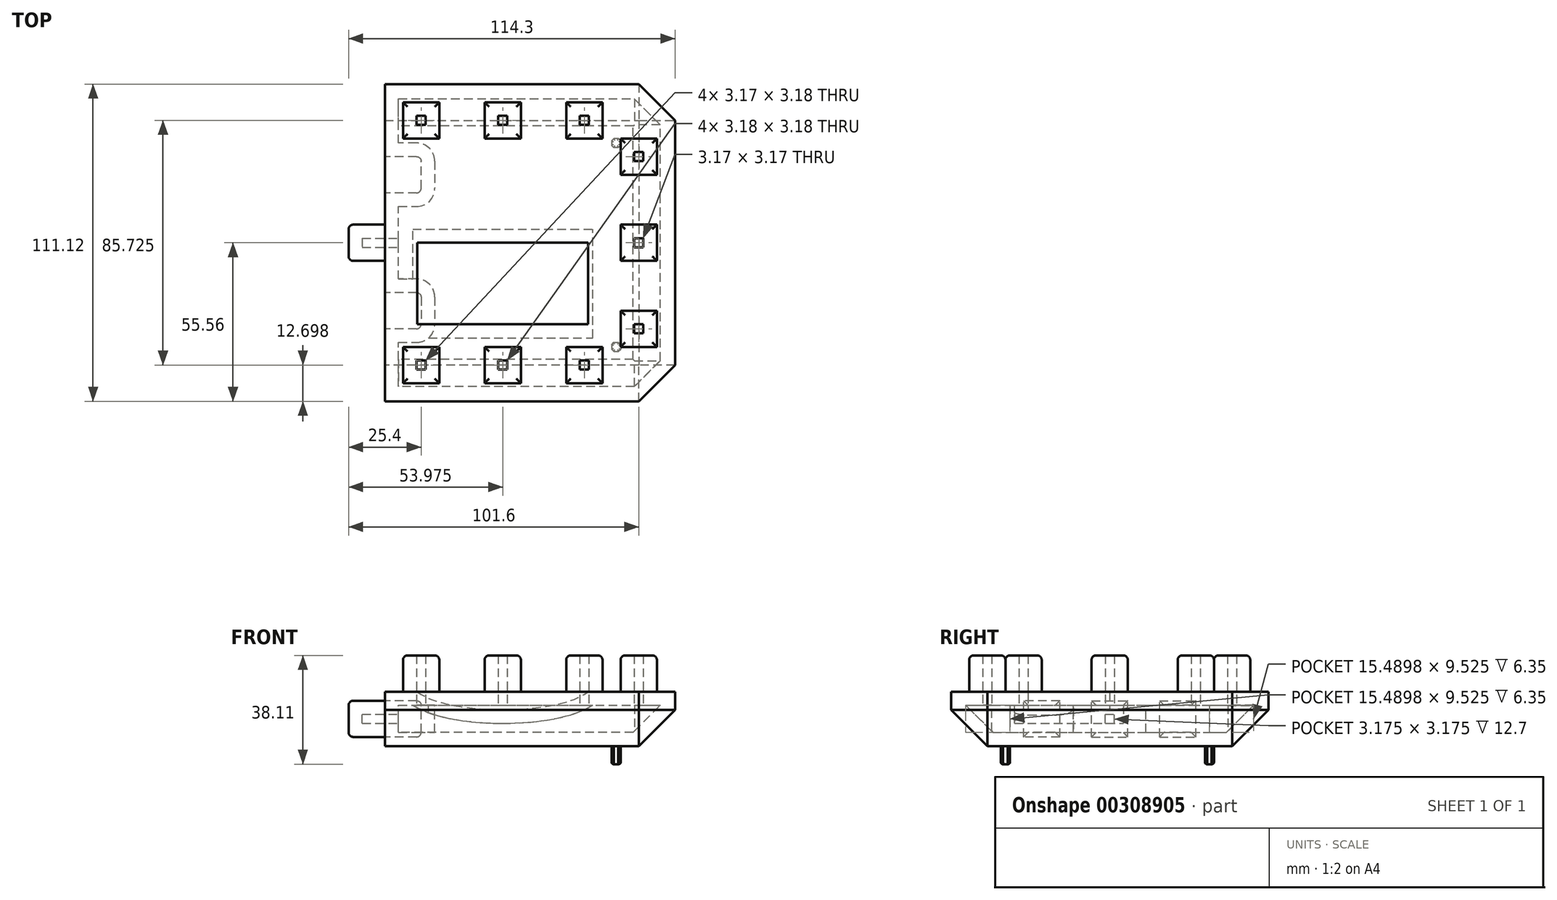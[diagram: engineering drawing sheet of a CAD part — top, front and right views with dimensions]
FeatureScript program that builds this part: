
annotation { "Feature Type Name" : "Feature", "Feature Type Description" : "" }
export const myFeature = defineFeature(function(context is Context, id is Id, definition is map)
    precondition{}
    {
        {
            var Q0;
            Q0=qCreatedBy(makeId("Front.planeOp"),FACE);
            var sketch = newSketch(context, id + "F0", { "sketchPlane" : qUnion([Q0])});
            skLineSegment(sketch, "E0.bottom", {"start": v(-50.8, -9.53) * mm, "end": v(50.8, -9.53) * mm});
            skLineSegment(sketch, "E0.top", {"start": v(-50.8, 9.53) * mm, "end": v(50.8, 9.53) * mm});
            skLineSegment(sketch, "E0.left", {"start": v(-50.8, -9.53) * mm, "end": v(-50.8, 9.53) * mm});
            skLineSegment(sketch, "E0.right", {"start": v(50.8, -9.53) * mm, "end": v(50.8, 9.53) * mm});
            skPoint(sketch, "E0.middle", {"position": v(0, 0) * mm});
            skSolve(sketch);
        }
        {
            var Q0;
            Q0=qSketchRegion(id+"F0",true);
            extrude(context, id + "F1", {"entities" : qUnion([Q0]), "endBound" : BoundingType.SYMMETRIC, "depth" : 111.12 * mm});
        }
        {
            var Q0;
            Q0=makeQuery(id+"F1.opExtrude","SWEPT_EDGE",EDGE,{"disambiguationData":[OSD([sQuery(id+"F0.wireOp",EDGE,"E0.bottom"),sQuery(id+"F0.wireOp",EDGE,"E0.right")])]});
            var Q1;
            Q1=makeQuery(id+"F1.opExtrude","CAP_EDGE",EDGE,{"disambiguationData":[OSD([sQuery(id+"F0.wireOp",EDGE,"E0.bottom")])],"isStart":false});
            var Q2;
            Q2=makeQuery(id+"F1.opExtrude","CAP_EDGE",EDGE,{"disambiguationData":[OSD([sQuery(id+"F0.wireOp",EDGE,"E0.bottom")])],"isStart":true});
            var Q3;
            Q3=makeQuery(id+"F1.opExtrude","CAP_EDGE",EDGE,{"disambiguationData":[OSD([sQuery(id+"F0.wireOp",EDGE,"E0.right")])],"isStart":false});
            var Q4;
            Q4=makeQuery(id+"F1.opExtrude","CAP_EDGE",EDGE,{"disambiguationData":[OSD([sQuery(id+"F0.wireOp",EDGE,"E0.right")])],"isStart":true});
            chamfer(context, id + "F2", {"entities" : qUnion([Q0, Q1, Q2, Q3, Q4]), "width" : 12.7 * mm, "tangentPropagation" : true});
        }
        {
            var Q0;
            Q0=makeQuery(id+"F1.opExtrude","SWEPT_FACE",FACE,{"disambiguationData":[OSD([sQuery(id+"F0.wireOp",EDGE,"E0.top")])]});
            var sketch = newSketch(context, id + "F3", { "sketchPlane" : qUnion([Q0])});
            skLineSegment(sketch, "E1.bottom", {"start": v(31.75, 23.81) * mm, "end": v(44.45, 23.81) * mm});
            skLineSegment(sketch, "E1.top", {"start": v(31.75, 36.51) * mm, "end": v(44.45, 36.51) * mm});
            skLineSegment(sketch, "E1.left", {"start": v(31.75, 23.81) * mm, "end": v(31.75, 36.51) * mm});
            skLineSegment(sketch, "E1.right", {"start": v(44.45, 23.81) * mm, "end": v(44.45, 36.51) * mm});
            skPoint(sketch, "E1.middle", {"position": v(38.1, 30.16) * mm});
            skLineSegment(sketch, "E2.bottom", {"start": v(31.75, -36.51) * mm, "end": v(44.45, -36.51) * mm});
            skLineSegment(sketch, "E2.top", {"start": v(31.75, -23.81) * mm, "end": v(44.45, -23.81) * mm});
            skLineSegment(sketch, "E2.left", {"start": v(31.75, -36.51) * mm, "end": v(31.75, -23.81) * mm});
            skLineSegment(sketch, "E2.right", {"start": v(44.45, -36.51) * mm, "end": v(44.45, -23.81) * mm});
            skPoint(sketch, "E2.middle", {"position": v(38.1, -30.16) * mm});
            skLineSegment(sketch, "E3.bottom", {"start": v(31.75, -6.35) * mm, "end": v(44.45, -6.35) * mm});
            skLineSegment(sketch, "E3.top", {"start": v(31.75, 6.35) * mm, "end": v(44.45, 6.35) * mm});
            skLineSegment(sketch, "E3.left", {"start": v(31.75, -6.35) * mm, "end": v(31.75, 6.35) * mm});
            skLineSegment(sketch, "E3.right", {"start": v(44.45, -6.35) * mm, "end": v(44.45, 6.35) * mm});
            skPoint(sketch, "E3.middle", {"position": v(38.1, 0) * mm});
            skLineSegment(sketch, "E4.bottom", {"start": v(12.7, 36.51) * mm, "end": v(25.4, 36.51) * mm});
            skLineSegment(sketch, "E4.top", {"start": v(12.7, 49.21) * mm, "end": v(25.4, 49.21) * mm});
            skLineSegment(sketch, "E4.left", {"start": v(12.7, 36.51) * mm, "end": v(12.7, 49.21) * mm});
            skLineSegment(sketch, "E4.right", {"start": v(25.4, 36.51) * mm, "end": v(25.4, 49.21) * mm});
            skPoint(sketch, "E4.middle", {"position": v(19.05, 42.86) * mm});
            skLineSegment(sketch, "E5.bottom", {"start": v(12.7, -36.51) * mm, "end": v(25.4, -36.51) * mm});
            skLineSegment(sketch, "E5.top", {"start": v(12.7, -49.21) * mm, "end": v(25.4, -49.21) * mm});
            skLineSegment(sketch, "E5.left", {"start": v(12.7, -36.51) * mm, "end": v(12.7, -49.21) * mm});
            skLineSegment(sketch, "E5.right", {"start": v(25.4, -36.51) * mm, "end": v(25.4, -49.21) * mm});
            skPoint(sketch, "E5.middle", {"position": v(19.05, -42.86) * mm});
            skLineSegment(sketch, "E6.bottom", {"start": v(-15.88, 36.51) * mm, "end": v(-3.17, 36.51) * mm});
            skLineSegment(sketch, "E6.top", {"start": v(-15.88, 49.21) * mm, "end": v(-3.17, 49.21) * mm});
            skLineSegment(sketch, "E6.left", {"start": v(-15.88, 36.51) * mm, "end": v(-15.88, 49.21) * mm});
            skLineSegment(sketch, "E6.right", {"start": v(-3.18, 36.51) * mm, "end": v(-3.18, 49.21) * mm});
            skPoint(sketch, "E6.middle", {"position": v(-9.53, 42.86) * mm});
            skLineSegment(sketch, "E7.bottom", {"start": v(-15.88, -36.51) * mm, "end": v(-3.17, -36.51) * mm});
            skLineSegment(sketch, "E7.top", {"start": v(-15.88, -49.21) * mm, "end": v(-3.17, -49.21) * mm});
            skLineSegment(sketch, "E7.left", {"start": v(-15.88, -36.51) * mm, "end": v(-15.88, -49.21) * mm});
            skLineSegment(sketch, "E7.right", {"start": v(-3.18, -36.51) * mm, "end": v(-3.18, -49.21) * mm});
            skPoint(sketch, "E7.middle", {"position": v(-9.52, -42.86) * mm});
            skLineSegment(sketch, "E8.bottom", {"start": v(-31.75, 36.51) * mm, "end": v(-44.45, 36.51) * mm});
            skLineSegment(sketch, "E8.top", {"start": v(-31.75, 49.21) * mm, "end": v(-44.45, 49.21) * mm});
            skLineSegment(sketch, "E8.left", {"start": v(-31.75, 36.51) * mm, "end": v(-31.75, 49.21) * mm});
            skLineSegment(sketch, "E8.right", {"start": v(-44.45, 36.51) * mm, "end": v(-44.45, 49.21) * mm});
            skPoint(sketch, "E8.middle", {"position": v(-38.1, 42.86) * mm});
            skPoint(sketch, "E8.middle.positionSnap0", {"position": v(-15.88, 42.86) * mm});
            skPoint(sketch, "E8.centerSnap0", {"position": v(-15.88, 42.86) * mm});
            skLineSegment(sketch, "E9.bottom", {"start": v(-31.75, -49.21) * mm, "end": v(-44.45, -49.21) * mm});
            skLineSegment(sketch, "E9.top", {"start": v(-31.75, -36.51) * mm, "end": v(-44.45, -36.51) * mm});
            skLineSegment(sketch, "E9.left", {"start": v(-31.75, -49.21) * mm, "end": v(-31.75, -36.51) * mm});
            skLineSegment(sketch, "E9.right", {"start": v(-44.45, -49.21) * mm, "end": v(-44.45, -36.51) * mm});
            skPoint(sketch, "E9.middle", {"position": v(-38.1, -42.86) * mm});
            skPoint(sketch, "E9.middle.positionSnap0", {"position": v(-15.88, -42.86) * mm});
            skPoint(sketch, "E9.centerSnap0", {"position": v(-15.88, -42.86) * mm});
            skSolve(sketch);
        }
        {
            var Q0;
            Q0=qSketchRegion(id+"F3",true);
            extrude(context, id + "F4", {"entities" : qUnion([Q0]), "operationType" : NewBodyOperationType.ADD, "depth" : 12.7 * mm});
        }
        {
            var Q0;
            Q0=makeQuery(id+"F1.opExtrude","SWEPT_FACE",FACE,{"disambiguationData":[OSD([sQuery(id+"F0.wireOp",EDGE,"E0.bottom")])]});
            var sketch = newSketch(context, id + "F5", { "sketchPlane" : qUnion([Q0])});
            skLineSegment(sketch, "E10.bottom", {"start": v(28.58, 34.93) * mm, "end": v(31.75, 34.93) * mm});
            skLineSegment(sketch, "E10.top", {"start": v(28.58, 38.1) * mm, "end": v(31.75, 38.1) * mm});
            skLineSegment(sketch, "E10.left", {"start": v(28.58, 34.93) * mm, "end": v(28.58, 38.1) * mm});
            skLineSegment(sketch, "E10.right", {"start": v(31.75, 34.93) * mm, "end": v(31.75, 38.1) * mm});
            skPoint(sketch, "E10.middle", {"position": v(30.16, 36.51) * mm});
            skLineSegment(sketch, "E11.bottom", {"start": v(31.75, -36.51) * mm, "end": v(28.58, -36.51) * mm});
            skLineSegment(sketch, "E11.top", {"start": v(31.75, -33.34) * mm, "end": v(28.58, -33.34) * mm});
            skLineSegment(sketch, "E11.left", {"start": v(31.75, -36.51) * mm, "end": v(31.75, -33.34) * mm});
            skLineSegment(sketch, "E11.right", {"start": v(28.58, -36.51) * mm, "end": v(28.58, -33.34) * mm});
            skPoint(sketch, "E11.middle", {"position": v(30.16, -34.92) * mm});
            skSolve(sketch);
        }
        {
            var Q0;
            Q0=qSketchRegion(id+"F5",true);
            extrude(context, id + "F6", {"entities" : qUnion([Q0]), "operationType" : NewBodyOperationType.ADD, "depth" : 6.35 * mm});
        }
        {
            var Q0;
            Q0=makeQuery(id+"F6.opExtrude","SWEPT_EDGE",EDGE,{"disambiguationData":[OSD([sQuery(id+"F5.wireOp",EDGE,"E11.bottom"),sQuery(id+"F5.wireOp",EDGE,"E11.right")])]});
            var Q1;
            Q1=makeQuery(id+"F6.opExtrude","SWEPT_EDGE",EDGE,{"disambiguationData":[OSD([sQuery(id+"F5.wireOp",EDGE,"E11.top"),sQuery(id+"F5.wireOp",EDGE,"E11.right")])]});
            var Q2;
            Q2=makeQuery(id+"F6.opExtrude","SWEPT_EDGE",EDGE,{"disambiguationData":[OSD([sQuery(id+"F5.wireOp",EDGE,"E11.top"),sQuery(id+"F5.wireOp",EDGE,"E11.left")])]});
            var Q3;
            Q3=makeQuery(id+"F6.opExtrude","SWEPT_EDGE",EDGE,{"disambiguationData":[OSD([sQuery(id+"F5.wireOp",EDGE,"E11.bottom"),sQuery(id+"F5.wireOp",EDGE,"E11.left")])]});
            var Q4;
            Q4=makeQuery(id+"F6.opExtrude","CAP_EDGE",EDGE,{"disambiguationData":[OSD([sQuery(id+"F5.wireOp",EDGE,"E11.left")])],"isStart":true});
            var Q5;
            Q5=makeQuery(id+"F6.opExtrude","SWEPT_EDGE",EDGE,{"disambiguationData":[OSD([sQuery(id+"F5.wireOp",EDGE,"E10.bottom"),sQuery(id+"F5.wireOp",EDGE,"E10.left")])]});
            var Q6;
            Q6=makeQuery(id+"F6.opExtrude","SWEPT_EDGE",EDGE,{"disambiguationData":[OSD([sQuery(id+"F5.wireOp",EDGE,"E10.bottom"),sQuery(id+"F5.wireOp",EDGE,"E10.right")])]});
            var Q7;
            Q7=makeQuery(id+"F6.opExtrude","SWEPT_EDGE",EDGE,{"disambiguationData":[OSD([sQuery(id+"F5.wireOp",EDGE,"E10.top"),sQuery(id+"F5.wireOp",EDGE,"E10.right")])]});
            var Q8;
            Q8=makeQuery(id+"F6.opExtrude","CAP_EDGE",EDGE,{"disambiguationData":[OSD([sQuery(id+"F5.wireOp",EDGE,"E10.right")])],"isStart":true});
            var Q9;
            Q9=makeQuery(id+"F6.opExtrude","SWEPT_EDGE",EDGE,{"disambiguationData":[OSD([sQuery(id+"F5.wireOp",EDGE,"E10.top"),sQuery(id+"F5.wireOp",EDGE,"E10.left")])]});
            chamfer(context, id + "F7", {"entities" : qUnion([Q0, Q1, Q2, Q3, Q4, Q5, Q6, Q7, Q8, Q9]), "width" : 0.8 * mm, "tangentPropagation" : true});
        }
        {
            var Q0;
            Q0=makeQuery(id+"F6.opExtrude","CAP_FACE",FACE,{"disambiguationData":[OSD([sQuery(id+"F5.wireOp",EDGE,"E10.bottom"),sQuery(id+"F5.wireOp",EDGE,"E10.top"),sQuery(id+"F5.wireOp",EDGE,"E10.left"),sQuery(id+"F5.wireOp",EDGE,"E10.right")])],"isStart":false});
            var Q1;
            Q1=makeQuery(id+"F6.opExtrude","CAP_FACE",FACE,{"disambiguationData":[OSD([sQuery(id+"F5.wireOp",EDGE,"E11.bottom"),sQuery(id+"F5.wireOp",EDGE,"E11.top"),sQuery(id+"F5.wireOp",EDGE,"E11.left"),sQuery(id+"F5.wireOp",EDGE,"E11.right")])],"isStart":false});
            fillet(context, id + "F8", {"entities" : qUnion([Q0, Q1]), "radius" : 0.64 * mm, "tangentPropagation" : true, "allowEdgeOverflow" : false});
        }
        {
            var Q0;
            Q0=makeQuery(id+"F1.opExtrude","SWEPT_FACE",FACE,{"disambiguationData":[OSD([sQuery(id+"F0.wireOp",EDGE,"E0.left")])]});
            var sketch = newSketch(context, id + "F9", { "sketchPlane" : qUnion([Q0])});
            skLineSegment(sketch, "E12.bottom", {"start": v(-17.46, -6.35) * mm, "end": v(-30.16, -6.35) * mm});
            skLineSegment(sketch, "E12.top", {"start": v(-17.46, 6.35) * mm, "end": v(-30.16, 6.35) * mm});
            skLineSegment(sketch, "E12.left", {"start": v(-17.46, -6.35) * mm, "end": v(-17.46, 6.35) * mm});
            skLineSegment(sketch, "E12.right", {"start": v(-30.16, -6.35) * mm, "end": v(-30.16, 6.35) * mm});
            skPoint(sketch, "E12.middle", {"position": v(-23.81, 0) * mm});
            skLineSegment(sketch, "E13.bottom", {"start": v(17.46, -6.35) * mm, "end": v(30.16, -6.35) * mm});
            skLineSegment(sketch, "E13.top", {"start": v(17.46, 6.35) * mm, "end": v(30.16, 6.35) * mm});
            skLineSegment(sketch, "E13.left", {"start": v(17.46, -6.35) * mm, "end": v(17.46, 6.35) * mm});
            skLineSegment(sketch, "E13.right", {"start": v(30.16, -6.35) * mm, "end": v(30.16, 6.35) * mm});
            skPoint(sketch, "E13.middle", {"position": v(23.81, 0) * mm});
            skLineSegment(sketch, "E14.bottom", {"start": v(6.35, -6.35) * mm, "end": v(-6.35, -6.35) * mm});
            skLineSegment(sketch, "E14.top", {"start": v(6.35, 6.35) * mm, "end": v(-6.35, 6.35) * mm});
            skLineSegment(sketch, "E14.left", {"start": v(6.35, -6.35) * mm, "end": v(6.35, 6.35) * mm});
            skLineSegment(sketch, "E14.right", {"start": v(-6.35, -6.35) * mm, "end": v(-6.35, 6.35) * mm});
            skPoint(sketch, "E14.middle", {"position": v(0, 0) * mm});
            skSolve(sketch);
        }
        {
            var Q0;
            Q0=makeQuery(id+"F9.imprint","IMPRINT",FACE,{"disambiguationData":[TD([[makeQuery(id+"F9.imprint","IMPRINT",EDGE,{"derivedFrom":sQuery(id+"F9.wireOp",EDGE,"E12.bottom")}),-1.0]])]});
            var Q1;
            Q1=makeQuery(id+"F9.imprint","IMPRINT",FACE,{"disambiguationData":[TD([[makeQuery(id+"F9.imprint","IMPRINT",EDGE,{"derivedFrom":sQuery(id+"F9.wireOp",EDGE,"E13.bottom")}),1.0]])]});
            extrude(context, id + "F10", {"entities" : qUnion([Q0, Q1]), "operationType" : NewBodyOperationType.REMOVE, "oppositeDirection" : true, "depth" : 12.7 * mm});
        }
        {
            var Q0;
            Q0=makeQuery(id+"F9.imprint","IMPRINT",FACE,{"disambiguationData":[TD([[makeQuery(id+"F9.imprint","IMPRINT",EDGE,{"derivedFrom":sQuery(id+"F9.wireOp",EDGE,"E14.bottom")}),-1.0]])]});
            extrude(context, id + "F11", {"entities" : qUnion([Q0]), "operationType" : NewBodyOperationType.ADD, "depth" : 12.7 * mm});
        }
        {
            var Q0;
            Q0=makeQuery(id+"F4.opExtrude","CAP_FACE",FACE,{"disambiguationData":[OSD([sQuery(id+"F3.wireOp",EDGE,"E1.bottom"),sQuery(id+"F3.wireOp",EDGE,"E1.top"),sQuery(id+"F3.wireOp",EDGE,"E1.left"),sQuery(id+"F3.wireOp",EDGE,"E1.right")])],"isStart":false});
            var Q1;
            Q1=makeQuery(id+"F4.opExtrude","CAP_FACE",FACE,{"disambiguationData":[OSD([sQuery(id+"F3.wireOp",EDGE,"E3.bottom"),sQuery(id+"F3.wireOp",EDGE,"E3.top"),sQuery(id+"F3.wireOp",EDGE,"E3.left"),sQuery(id+"F3.wireOp",EDGE,"E3.right")])],"isStart":false});
            var Q2;
            Q2=makeQuery(id+"F4.opExtrude","CAP_FACE",FACE,{"disambiguationData":[OSD([sQuery(id+"F3.wireOp",EDGE,"E2.bottom"),sQuery(id+"F3.wireOp",EDGE,"E2.top"),sQuery(id+"F3.wireOp",EDGE,"E2.left"),sQuery(id+"F3.wireOp",EDGE,"E2.right")])],"isStart":false});
            var Q3;
            Q3=makeQuery(id+"F4.opExtrude","CAP_FACE",FACE,{"disambiguationData":[OSD([sQuery(id+"F3.wireOp",EDGE,"E4.bottom"),sQuery(id+"F3.wireOp",EDGE,"E4.top"),sQuery(id+"F3.wireOp",EDGE,"E4.left"),sQuery(id+"F3.wireOp",EDGE,"E4.right")])],"isStart":false});
            var Q4;
            Q4=makeQuery(id+"F4.opExtrude","CAP_FACE",FACE,{"disambiguationData":[OSD([sQuery(id+"F3.wireOp",EDGE,"E6.bottom"),sQuery(id+"F3.wireOp",EDGE,"E6.top"),sQuery(id+"F3.wireOp",EDGE,"E6.left"),sQuery(id+"F3.wireOp",EDGE,"E6.right")])],"isStart":false});
            var Q5;
            Q5=makeQuery(id+"F4.opExtrude","CAP_FACE",FACE,{"disambiguationData":[OSD([sQuery(id+"F3.wireOp",EDGE,"E7.bottom"),sQuery(id+"F3.wireOp",EDGE,"E7.top"),sQuery(id+"F3.wireOp",EDGE,"E7.left"),sQuery(id+"F3.wireOp",EDGE,"E7.right")])],"isStart":false});
            var Q6;
            Q6=makeQuery(id+"F4.opExtrude","CAP_FACE",FACE,{"disambiguationData":[OSD([sQuery(id+"F3.wireOp",EDGE,"E5.bottom"),sQuery(id+"F3.wireOp",EDGE,"E5.top"),sQuery(id+"F3.wireOp",EDGE,"E5.left"),sQuery(id+"F3.wireOp",EDGE,"E5.right")])],"isStart":false});
            var Q7;
            Q7=makeQuery(id+"F4.opExtrude","CAP_FACE",FACE,{"disambiguationData":[OSD([sQuery(id+"F3.wireOp",EDGE,"E9.bottom"),sQuery(id+"F3.wireOp",EDGE,"E9.top"),sQuery(id+"F3.wireOp",EDGE,"E9.left"),sQuery(id+"F3.wireOp",EDGE,"E9.right")])],"isStart":false});
            var Q8;
            Q8=makeQuery(id+"F4.opExtrude","CAP_FACE",FACE,{"disambiguationData":[OSD([sQuery(id+"F3.wireOp",EDGE,"E8.bottom"),sQuery(id+"F3.wireOp",EDGE,"E8.top"),sQuery(id+"F3.wireOp",EDGE,"E8.left"),sQuery(id+"F3.wireOp",EDGE,"E8.right")])],"isStart":false});
            var Q9;
            Q9=makeQuery(id+"F10.boolean.opBoolean","COPY",FACE,{"derivedFrom":makeQuery(id+"F10.opExtrude","CAP_FACE",FACE,{"disambiguationData":[OSD([sQuery(id+"F9.wireOp",EDGE,"E12.bottom"),sQuery(id+"F9.wireOp",EDGE,"E12.top"),sQuery(id+"F9.wireOp",EDGE,"E12.left"),sQuery(id+"F9.wireOp",EDGE,"E12.right")])],"isStart":false})});
            var Q10;
            Q10=makeQuery(id+"F11.opExtrude","CAP_FACE",FACE,{"disambiguationData":[OSD([sQuery(id+"F9.wireOp",EDGE,"E14.bottom"),sQuery(id+"F9.wireOp",EDGE,"E14.top"),sQuery(id+"F9.wireOp",EDGE,"E14.left"),sQuery(id+"F9.wireOp",EDGE,"E14.right")])],"isStart":false});
            var Q11;
            Q11=makeQuery(id+"F10.boolean.opBoolean","COPY",FACE,{"derivedFrom":makeQuery(id+"F10.opExtrude","CAP_FACE",FACE,{"disambiguationData":[OSD([sQuery(id+"F9.wireOp",EDGE,"E13.bottom"),sQuery(id+"F9.wireOp",EDGE,"E13.top"),sQuery(id+"F9.wireOp",EDGE,"E13.left"),sQuery(id+"F9.wireOp",EDGE,"E13.right")])],"isStart":false})});
            fillet(context, id + "F12", {"entities" : qUnion([Q0, Q1, Q2, Q3, Q4, Q5, Q6, Q7, Q8, Q9, Q10, Q11]), "radius" : 1.59 * mm, "tangentPropagation" : true, "allowEdgeOverflow" : false});
        }
        {
            var Q0;
            Q0=qCreatedBy(makeId("Front.planeOp"),FACE);
            var sketch = newSketch(context, id + "F13", { "sketchPlane" : qUnion([Q0])});
            skEllipse(sketch, "E15", {"center": v(-9.53, 12.7) * mm, "majorRadius": 31.75 * mm, "minorRadius": 9.53 * mm, "majorAxis": v(1, 0)});
            skSolve(sketch);
        }
        {
            var Q0;
            Q0=makeQuery(id+"F13.imprint","IMPRINT",FACE,{"disambiguationData":[TD([[makeQuery(id+"F13.imprint","IMPRINT",EDGE,{"derivedFrom":sQuery(id+"F13.wireOp",EDGE,"E15")}),1.0]])]});
            extrude(context, id + "F14", {"entities" : qUnion([Q0]), "operationType" : NewBodyOperationType.REMOVE, "depth" : 28.57 * mm});
        }
        {
            var Q0;
            Q0=makeQuery(id+"F4.opExtrude","CAP_FACE",FACE,{"disambiguationData":[OSD([sQuery(id+"F3.wireOp",EDGE,"E5.bottom"),sQuery(id+"F3.wireOp",EDGE,"E5.top"),sQuery(id+"F3.wireOp",EDGE,"E5.left"),sQuery(id+"F3.wireOp",EDGE,"E5.right")])],"isStart":false});
            var Q1;
            Q1=makeQuery(id+"F4.opExtrude","CAP_FACE",FACE,{"disambiguationData":[OSD([sQuery(id+"F3.wireOp",EDGE,"E7.bottom"),sQuery(id+"F3.wireOp",EDGE,"E7.top"),sQuery(id+"F3.wireOp",EDGE,"E7.left"),sQuery(id+"F3.wireOp",EDGE,"E7.right")])],"isStart":false});
            var Q2;
            Q2=makeQuery(id+"F4.opExtrude","CAP_FACE",FACE,{"disambiguationData":[OSD([sQuery(id+"F3.wireOp",EDGE,"E9.bottom"),sQuery(id+"F3.wireOp",EDGE,"E9.top"),sQuery(id+"F3.wireOp",EDGE,"E9.left"),sQuery(id+"F3.wireOp",EDGE,"E9.right")])],"isStart":false});
            var Q3;
            Q3=makeQuery(id+"F4.opExtrude","CAP_FACE",FACE,{"disambiguationData":[OSD([sQuery(id+"F3.wireOp",EDGE,"E2.bottom"),sQuery(id+"F3.wireOp",EDGE,"E2.top"),sQuery(id+"F3.wireOp",EDGE,"E2.left"),sQuery(id+"F3.wireOp",EDGE,"E2.right")])],"isStart":false});
            var Q4;
            Q4=makeQuery(id+"F4.opExtrude","CAP_FACE",FACE,{"disambiguationData":[OSD([sQuery(id+"F3.wireOp",EDGE,"E3.bottom"),sQuery(id+"F3.wireOp",EDGE,"E3.top"),sQuery(id+"F3.wireOp",EDGE,"E3.left"),sQuery(id+"F3.wireOp",EDGE,"E3.right")])],"isStart":false});
            var Q5;
            Q5=makeQuery(id+"F4.opExtrude","CAP_FACE",FACE,{"disambiguationData":[OSD([sQuery(id+"F3.wireOp",EDGE,"E1.bottom"),sQuery(id+"F3.wireOp",EDGE,"E1.top"),sQuery(id+"F3.wireOp",EDGE,"E1.left"),sQuery(id+"F3.wireOp",EDGE,"E1.right")])],"isStart":false});
            var Q6;
            Q6=makeQuery(id+"F4.opExtrude","CAP_FACE",FACE,{"disambiguationData":[OSD([sQuery(id+"F3.wireOp",EDGE,"E4.bottom"),sQuery(id+"F3.wireOp",EDGE,"E4.top"),sQuery(id+"F3.wireOp",EDGE,"E4.left"),sQuery(id+"F3.wireOp",EDGE,"E4.right")])],"isStart":false});
            var Q7;
            Q7=makeQuery(id+"F4.opExtrude","CAP_FACE",FACE,{"disambiguationData":[OSD([sQuery(id+"F3.wireOp",EDGE,"E6.bottom"),sQuery(id+"F3.wireOp",EDGE,"E6.top"),sQuery(id+"F3.wireOp",EDGE,"E6.left"),sQuery(id+"F3.wireOp",EDGE,"E6.right")])],"isStart":false});
            var Q8;
            Q8=makeQuery(id+"F4.opExtrude","CAP_FACE",FACE,{"disambiguationData":[OSD([sQuery(id+"F3.wireOp",EDGE,"E8.bottom"),sQuery(id+"F3.wireOp",EDGE,"E8.top"),sQuery(id+"F3.wireOp",EDGE,"E8.left"),sQuery(id+"F3.wireOp",EDGE,"E8.right")])],"isStart":false});
            shell(context, id + "F15", {"entities" : qUnion([Q0, Q1, Q2, Q3, Q4, Q5, Q6, Q7, Q8]), "thickness" : 4.76 * mm});
        }
    });
